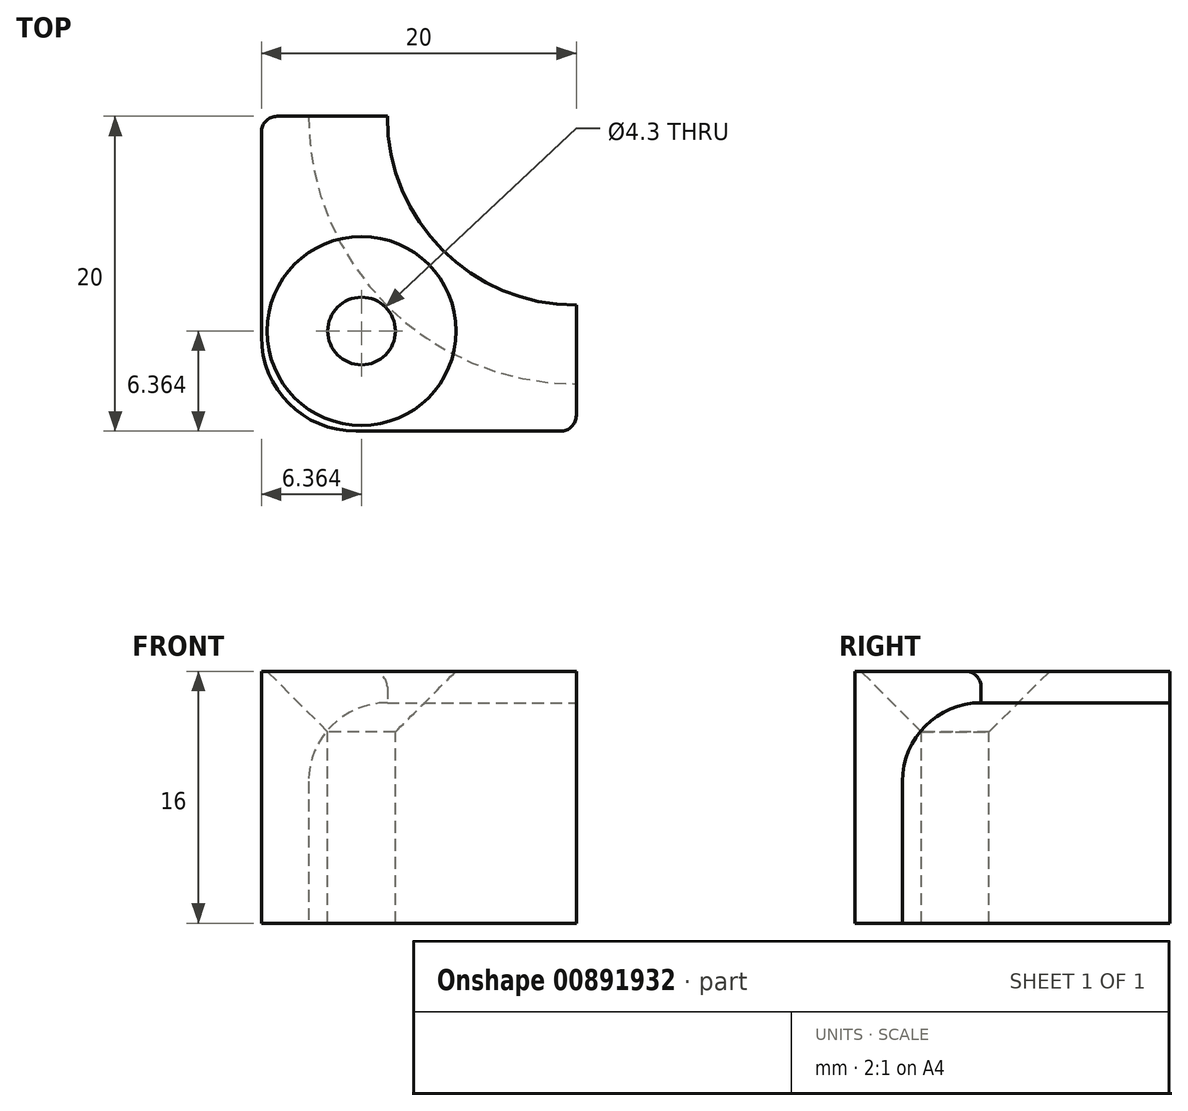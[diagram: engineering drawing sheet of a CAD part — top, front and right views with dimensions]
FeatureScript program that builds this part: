
annotation { "Feature Type Name" : "Feature", "Feature Type Description" : "" }
export const myFeature = defineFeature(function(context is Context, id is Id, definition is map)
    precondition{}
    {
        {
            var Q0;
            Q0=qCreatedBy(makeId("Top.planeOp"),FACE);
            var sketch = newSketch(context, id + "F0", { "sketchPlane" : qUnion([Q0])});
            skLineSegment(sketch, "E0.bottom", {"start": v(0, 0) * mm, "end": v(20, 0) * mm});
            skLineSegment(sketch, "E0.top", {"start": v(0, 20) * mm, "end": v(20, 20) * mm});
            skLineSegment(sketch, "E0.left", {"start": v(0, 0) * mm, "end": v(0, 20) * mm});
            skLineSegment(sketch, "E0.right", {"start": v(20, 0) * mm, "end": v(20, 20) * mm});
            skArc(sketch, "E1", {"start": v(3, 20) * mm, "mid": v(7.98, 7.98) * mm, "end": v(20, 3) * mm});
            skLineSegment(sketch, "E2", {"start": v(0, 0) * mm, "end": v(20, 20) * mm, "construction": true});
            skLineSegment(sketch, "E3", {"start": v(3, 20) * mm, "end": v(3, 44.66) * mm, "construction": true});
            skArc(sketch, "E4.0", {"start": v(8, 20) * mm, "mid": v(11.51, 11.51) * mm, "end": v(20, 8) * mm});
            skPoint(sketch, "E5", {"position": v(4.95, 4.95) * mm});
            skSolve(sketch);
        }
        {
            var Q0;
            {var subQ4=sQuery(id+"F0.wireOp",EDGE,"E0.bottom");Q0=makeQuery(id+"F0.imprint","IMPRINT",FACE,{"disambiguationData":[TD([[makeQuery(id+"F0.imprint","IMPRINT",EDGE,{"derivedFrom":subQ4}),1.0]])]});}
            var Q1;
            {var subQ0=sQuery(id+"F0.wireOp",EDGE,"E1");Q1=makeQuery(id+"F0.imprint","IMPRINT",FACE,{"disambiguationData":[TD([[makeQuery(id+"F0.imprint","IMPRINT",EDGE,{"derivedFrom":subQ0}),1.0]])]});}
            extrude(context, id + "F1", {"entities" : qUnion([Q0, Q1]), "depth" : 16 * mm, "offsetDistance" : 25 * mm});
        }
        {
            var Q0;
            {var subQ0=sQuery(id+"F0.wireOp",EDGE,"E1");Q0=makeQuery(id+"F0.imprint","IMPRINT",FACE,{"disambiguationData":[TD([[makeQuery(id+"F0.imprint","IMPRINT",EDGE,{"derivedFrom":subQ0}),1.0]])]});}
            extrude(context, id + "F2", {"entities" : qUnion([Q0]), "operationType" : NewBodyOperationType.REMOVE, "depth" : 14 * mm, "offsetDistance" : 25 * mm});
        }
        {
            var Q0;
            Q0=makeQuery(id+"F2.boolean.opBoolean","COPY",EDGE,{"derivedFrom":makeQuery(id+"F2.opExtrude","CAP_EDGE",EDGE,{"disambiguationData":[OSD([sQuery(id+"F0.wireOp",EDGE,"E1")])],"isStart":false})});
            fillet(context, id + "F3", {"entities" : qUnion([Q0]), "radius" : 5 * mm, "tangentPropagation" : true, "allowEdgeOverflow" : false});
        }
        {
            var Q0;
            Q0=makeQuery(id+"F1.opExtrude","CAP_FACE",FACE,{"disambiguationData":[OSD([sQuery(id+"F0.wireOp",EDGE,"E0.bottom"),sQuery(id+"F0.wireOp",EDGE,"E0.top"),sQuery(id+"F0.wireOp",EDGE,"E0.left"),sQuery(id+"F0.wireOp",EDGE,"E0.right"),sQuery(id+"F0.wireOp",EDGE,"E4.0")])],"isStart":false});
            var sketch = newSketch(context, id + "F4", { "sketchPlane" : qUnion([Q0])});
            skPoint(sketch, "E6", {"position": v(6.36, 6.36) * mm});
            skSolve(sketch);
        }
        {
            var Q0;
            Q0=sQuery(id+"F0.wireOp",VERTEX,"E5");
            var Q1;
            Q1=sQuery(id+"F4.wireOp",VERTEX,"E6");
            var Q2;
            Q2=makeQuery(id+"F1.opExtrude","SWEPT_BODY",BODY,{"disambiguationData":[OSD([sQuery(id+"F0.wireOp",EDGE,"E0.bottom"),sQuery(id+"F0.wireOp",EDGE,"E0.top"),sQuery(id+"F0.wireOp",EDGE,"E0.left"),sQuery(id+"F0.wireOp",EDGE,"E0.right"),sQuery(id+"F0.wireOp",EDGE,"E4.0")])]});
            hole(context, id + "F5", {"style" : HoleStyle.C_SINK, "endStyle" : HoleEndStyle.THROUGH, "holeDiameter" : 4.3 * mm, "cSinkDiameter" : 12 * mm, "cSinkAngle" : 90 * degree, "majorDiameter" : 5 * mm, "isTappedThrough" : true, "tappedDepth" : 12 * mm, "tapClearance" : 3, "startFromSketch" : true, "locations" : qUnion([Q0, Q1]), "scope" : qUnion([Q2])});
        }
        {
            var Q0;
            Q0=makeQuery(id+"F1.opExtrude","SWEPT_EDGE",EDGE,{"disambiguationData":[OSD([sQuery(id+"F0.wireOp",EDGE,"E0.bottom"),sQuery(id+"F0.wireOp",EDGE,"E0.left")])]});
            fillet(context, id + "F6", {"entities" : qUnion([Q0]), "radius" : 6 * mm, "tangentPropagation" : true, "allowEdgeOverflow" : false});
        }
        {
            var Q0;
            Q0=makeQuery(id+"F1.opExtrude","SWEPT_EDGE",EDGE,{"disambiguationData":[OSD([sQuery(id+"F0.wireOp",EDGE,"E0.bottom"),sQuery(id+"F0.wireOp",EDGE,"E0.right")])]});
            var Q1;
            Q1=makeQuery(id+"F1.opExtrude","SWEPT_EDGE",EDGE,{"disambiguationData":[OSD([sQuery(id+"F0.wireOp",EDGE,"E0.top"),sQuery(id+"F0.wireOp",EDGE,"E0.left")])]});
            var Q2;
            Q2=makeQuery(id+"F1.opExtrude","CAP_EDGE",EDGE,{"disambiguationData":[OSD([sQuery(id+"F0.wireOp",EDGE,"E4.0")])],"isStart":false});
            fillet(context, id + "F7", {"entities" : qUnion([Q0, Q1, Q2]), "radius" : 1 * mm, "tangentPropagation" : true, "allowEdgeOverflow" : false});
        }
    });
